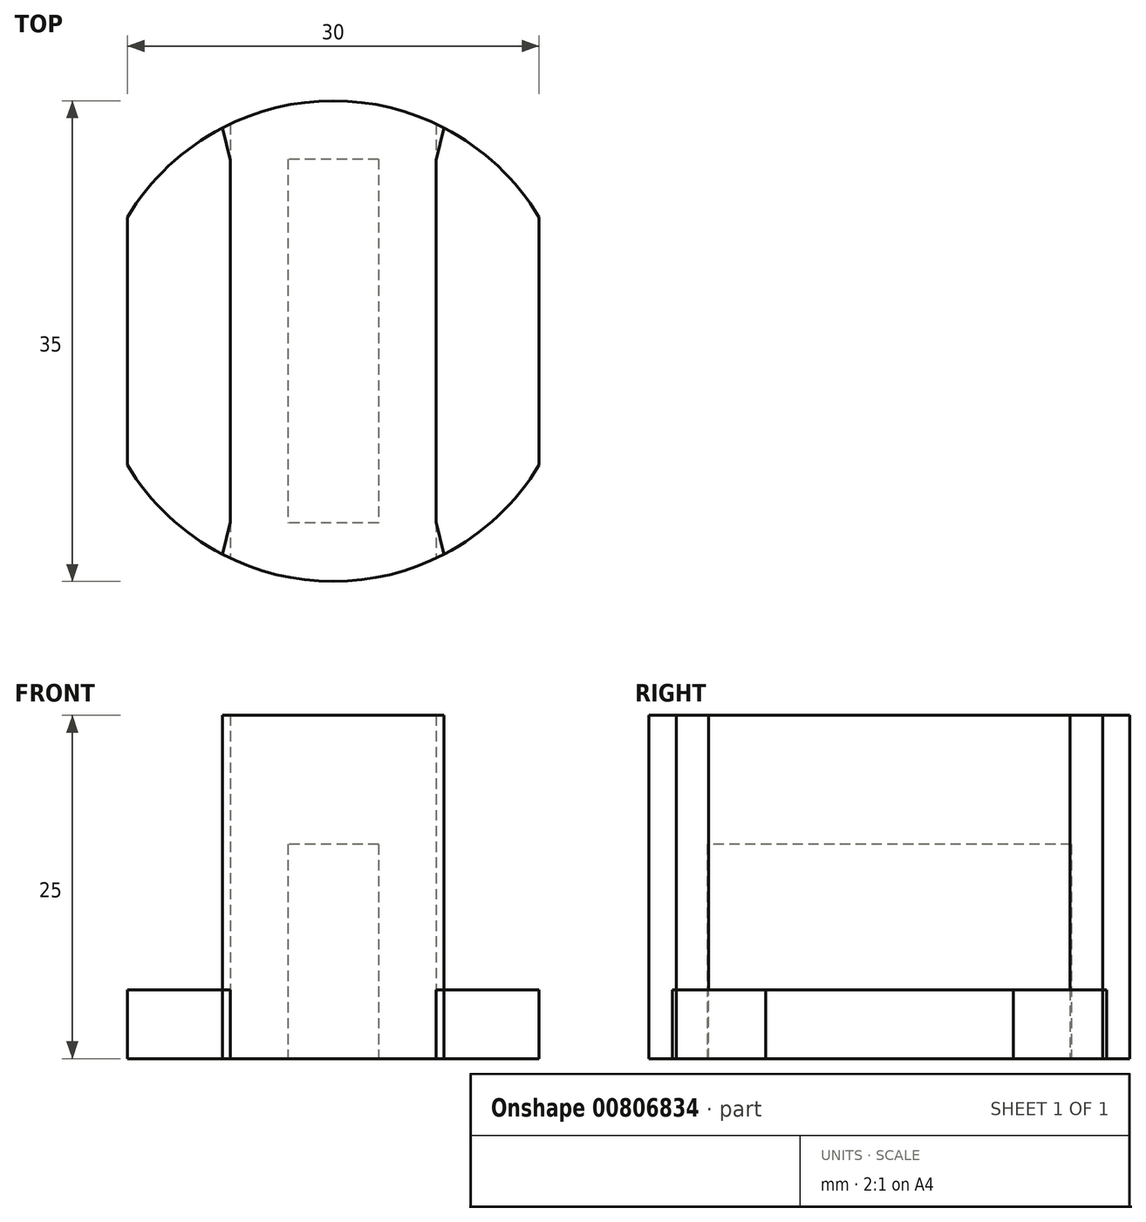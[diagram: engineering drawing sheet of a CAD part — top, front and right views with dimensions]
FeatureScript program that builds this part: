
annotation { "Feature Type Name" : "Feature", "Feature Type Description" : "" }
export const myFeature = defineFeature(function(context is Context, id is Id, definition is map)
    precondition{}
    {
        {
            var Q0;
            Q0=qCreatedBy(makeId("Top.planeOp"),FACE);
            var sketch = newSketch(context, id + "F0", { "sketchPlane" : qUnion([Q0])});
            skCircle(sketch, "E0", {"center": v(0, 0) * mm, "radius": 17.5 * mm});
            skLineSegment(sketch, "E1.bottom", {"start": v(7.5, 20) * mm, "end": v(-7.5, 20) * mm});
            skLineSegment(sketch, "E1.top", {"start": v(7.5, -20) * mm, "end": v(-7.5, -20) * mm});
            skLineSegment(sketch, "E1.left", {"start": v(7.5, 20) * mm, "end": v(7.5, -20) * mm});
            skLineSegment(sketch, "E1.right", {"start": v(-7.5, 20) * mm, "end": v(-7.5, -20) * mm});
            skLineSegment(sketch, "E2.bottom", {"start": v(3.3, 13.25) * mm, "end": v(-3.3, 13.25) * mm});
            skLineSegment(sketch, "E2.top", {"start": v(3.3, -13.25) * mm, "end": v(-3.3, -13.25) * mm});
            skLineSegment(sketch, "E2.left", {"start": v(3.3, 13.25) * mm, "end": v(3.3, -13.25) * mm});
            skLineSegment(sketch, "E2.right", {"start": v(-3.3, 13.25) * mm, "end": v(-3.3, -13.25) * mm});
            skLineSegment(sketch, "E3.bottom", {"start": v(15, 20) * mm, "end": v(-15, 20) * mm});
            skLineSegment(sketch, "E3.top", {"start": v(15, -20) * mm, "end": v(-15, -20) * mm});
            skLineSegment(sketch, "E3.left", {"start": v(15, 20) * mm, "end": v(15, -20) * mm});
            skLineSegment(sketch, "E3.right", {"start": v(-15, 20) * mm, "end": v(-15, -20) * mm});
            skLineSegment(sketch, "E4.bottom", {"start": v(23.86, 11.75) * mm, "end": v(-23.86, 11.75) * mm});
            skLineSegment(sketch, "E4.top", {"start": v(23.86, -11.75) * mm, "end": v(-23.86, -11.75) * mm});
            skLineSegment(sketch, "E4.left", {"start": v(23.86, 11.75) * mm, "end": v(23.86, -11.75) * mm});
            skLineSegment(sketch, "E4.right", {"start": v(-23.86, 11.75) * mm, "end": v(-23.86, -11.75) * mm});
            skSolve(sketch);
        }
        {
            var Q0;
            {var subQ0=sQuery(id+"F0.wireOp",EDGE,"E3.left");var subQ1=sQuery(id+"F0.wireOp",EDGE,"E0");var subQ2=makeQuery(id+"F0.imprint","INTERSECT",VERTEX,{"disambiguationData":[OD(0.0)],"derivedFrom":[subQ1,subQ0]});Q0=makeQuery(id+"F0.imprint","IMPRINT",FACE,{"disambiguationData":[TD([[makeQuery(id+"F0.imprint","IMPRINT",EDGE,{"disambiguationData":[TD([[subQ2,-1.0]])],"derivedFrom":subQ1}),1.0]])]});}
            var Q1;
            {var subQ0=sQuery(id+"F0.wireOp",EDGE,"E3.right");var subQ1=sQuery(id+"F0.wireOp",EDGE,"E0");var subQ2=makeQuery(id+"F0.imprint","INTERSECT",VERTEX,{"disambiguationData":[OD(0.0)],"derivedFrom":[subQ1,subQ0]});Q1=makeQuery(id+"F0.imprint","IMPRINT",FACE,{"disambiguationData":[TD([[makeQuery(id+"F0.imprint","IMPRINT",EDGE,{"disambiguationData":[TD([[subQ2,1.0]])],"derivedFrom":subQ1}),1.0]])]});}
            var Q2;
            {var subQ0=sQuery(id+"F0.wireOp",EDGE,"E1.right");var subQ1=sQuery(id+"F0.wireOp",EDGE,"E0");var subQ2=makeQuery(id+"F0.imprint","INTERSECT",VERTEX,{"disambiguationData":[OD(0.0)],"derivedFrom":[subQ1,subQ0]});Q2=makeQuery(id+"F0.imprint","IMPRINT",FACE,{"disambiguationData":[TD([[makeQuery(id+"F0.imprint","IMPRINT",EDGE,{"disambiguationData":[TD([[subQ2,-1.0]])],"derivedFrom":subQ1}),1.0]])]});}
            var Q3;
            {var subQ0=sQuery(id+"F0.wireOp",EDGE,"E1.left");var subQ1=sQuery(id+"F0.wireOp",EDGE,"E0");var subQ2=makeQuery(id+"F0.imprint","INTERSECT",VERTEX,{"disambiguationData":[OD(1.0)],"derivedFrom":[subQ1,subQ0]});Q3=makeQuery(id+"F0.imprint","IMPRINT",FACE,{"disambiguationData":[TD([[makeQuery(id+"F0.imprint","IMPRINT",EDGE,{"disambiguationData":[TD([[subQ2,-1.0]])],"derivedFrom":subQ1}),1.0]])]});}
            var Q4;
            {var subQ0=sQuery(id+"F0.wireOp",EDGE,"E4.top");var subQ1=sQuery(id+"F0.wireOp",EDGE,"E0");var subQ2=makeQuery(id+"F0.imprint","INTERSECT",VERTEX,{"disambiguationData":[OD(0.0)],"derivedFrom":[subQ1,subQ0]});Q4=makeQuery(id+"F0.imprint","IMPRINT",FACE,{"disambiguationData":[TD([[makeQuery(id+"F0.imprint","IMPRINT",EDGE,{"disambiguationData":[TD([[subQ2,-1.0]])],"derivedFrom":subQ1}),1.0]])]});}
            var Q5;
            {var subQ0=sQuery(id+"F0.wireOp",EDGE,"E4.bottom");var subQ1=sQuery(id+"F0.wireOp",EDGE,"E0");var subQ2=makeQuery(id+"F0.imprint","INTERSECT",VERTEX,{"disambiguationData":[OD(0.0)],"derivedFrom":[subQ1,subQ0]});Q5=makeQuery(id+"F0.imprint","IMPRINT",FACE,{"disambiguationData":[TD([[makeQuery(id+"F0.imprint","IMPRINT",EDGE,{"disambiguationData":[TD([[subQ2,-1.0]])],"derivedFrom":subQ1}),1.0]])]});}
            extrude(context, id + "F1", {"entities" : qUnion([Q0, Q1, Q2, Q3, Q4, Q5]), "depth" : 5 * mm, "offsetDistance" : 25 * mm});
        }
        {
            var Q0;
            Q0=makeQuery(id+"F0.imprint","IMPRINT",FACE,{"disambiguationData":[TD([[makeQuery(id+"F0.imprint","IMPRINT",EDGE,{"derivedFrom":sQuery(id+"F0.wireOp",EDGE,"E2.bottom")}),1.0]])]});
            var Q1;
            Q1=makeQuery(id+"F0.imprint","IMPRINT",FACE,{"disambiguationData":[TD([[makeQuery(id+"F0.imprint","IMPRINT",EDGE,{"derivedFrom":sQuery(id+"F0.wireOp",EDGE,"E2.bottom")}),-1.0]])]});
            var Q2;
            {var subQ0=sQuery(id+"F0.wireOp",EDGE,"E4.bottom");var subQ1=sQuery(id+"F0.wireOp",EDGE,"E1.right");var subQ2=makeQuery(id+"F0.imprint","INTERSECT",VERTEX,{"derivedFrom":[subQ1,subQ0]});Q2=makeQuery(id+"F0.imprint","IMPRINT",FACE,{"disambiguationData":[TD([[makeQuery(id+"F0.imprint","IMPRINT",EDGE,{"disambiguationData":[TD([[subQ2,-1.0]])],"derivedFrom":subQ1}),1.0]])]});}
            var Q3;
            {var subQ9=sQuery(id+"F0.wireOp",EDGE,"E2.top");Q3=makeQuery(id+"F0.imprint","IMPRINT",FACE,{"disambiguationData":[TD([[makeQuery(id+"F0.imprint","IMPRINT",EDGE,{"derivedFrom":subQ9}),1.0]])]});}
            var Q4;
            {var subQ0=sQuery(id+"F0.wireOp",EDGE,"E4.bottom");var subQ1=sQuery(id+"F0.wireOp",EDGE,"E1.left");var subQ2=makeQuery(id+"F0.imprint","INTERSECT",VERTEX,{"derivedFrom":[subQ1,subQ0]});Q4=makeQuery(id+"F0.imprint","IMPRINT",FACE,{"disambiguationData":[TD([[makeQuery(id+"F0.imprint","IMPRINT",EDGE,{"disambiguationData":[TD([[subQ2,-1.0]])],"derivedFrom":subQ1}),-1.0]])]});}
            var Q5;
            {var subQ0=sQuery(id+"F0.wireOp",EDGE,"E4.bottom");var subQ1=sQuery(id+"F0.wireOp",EDGE,"E2.left");var subQ2=makeQuery(id+"F0.imprint","INTERSECT",VERTEX,{"derivedFrom":[subQ1,subQ0]});Q5=makeQuery(id+"F0.imprint","IMPRINT",FACE,{"disambiguationData":[TD([[makeQuery(id+"F0.imprint","IMPRINT",EDGE,{"disambiguationData":[TD([[subQ2,-1.0]])],"derivedFrom":subQ1}),-1.0]])]});}
            var Q6;
            {var subQ0=sQuery(id+"F0.wireOp",EDGE,"E2.top");Q6=makeQuery(id+"F0.imprint","IMPRINT",FACE,{"disambiguationData":[TD([[makeQuery(id+"F0.imprint","IMPRINT",EDGE,{"derivedFrom":subQ0}),-1.0]])]});}
            var Q7;
            {var subQ0=sQuery(id+"F0.wireOp",EDGE,"E4.top");var subQ1=sQuery(id+"F0.wireOp",EDGE,"E0");var subQ2=makeQuery(id+"F0.imprint","INTERSECT",VERTEX,{"disambiguationData":[OD(0.0)],"derivedFrom":[subQ1,subQ0]});Q7=makeQuery(id+"F0.imprint","IMPRINT",FACE,{"disambiguationData":[TD([[makeQuery(id+"F0.imprint","IMPRINT",EDGE,{"disambiguationData":[TD([[subQ2,-1.0]])],"derivedFrom":subQ1}),1.0]])]});}
            var Q8;
            {var subQ0=sQuery(id+"F0.wireOp",EDGE,"E1.right");var subQ1=sQuery(id+"F0.wireOp",EDGE,"E0");var subQ2=makeQuery(id+"F0.imprint","INTERSECT",VERTEX,{"disambiguationData":[OD(0.0)],"derivedFrom":[subQ1,subQ0]});Q8=makeQuery(id+"F0.imprint","IMPRINT",FACE,{"disambiguationData":[TD([[makeQuery(id+"F0.imprint","IMPRINT",EDGE,{"disambiguationData":[TD([[subQ2,-1.0]])],"derivedFrom":subQ1}),1.0]])]});}
            var Q9;
            {var subQ0=sQuery(id+"F0.wireOp",EDGE,"E4.bottom");var subQ1=sQuery(id+"F0.wireOp",EDGE,"E0");var subQ2=makeQuery(id+"F0.imprint","INTERSECT",VERTEX,{"disambiguationData":[OD(0.0)],"derivedFrom":[subQ1,subQ0]});Q9=makeQuery(id+"F0.imprint","IMPRINT",FACE,{"disambiguationData":[TD([[makeQuery(id+"F0.imprint","IMPRINT",EDGE,{"disambiguationData":[TD([[subQ2,-1.0]])],"derivedFrom":subQ1}),1.0]])]});}
            var Q10;
            {var subQ0=sQuery(id+"F0.wireOp",EDGE,"E1.left");var subQ1=sQuery(id+"F0.wireOp",EDGE,"E0");var subQ2=makeQuery(id+"F0.imprint","INTERSECT",VERTEX,{"disambiguationData":[OD(1.0)],"derivedFrom":[subQ1,subQ0]});Q10=makeQuery(id+"F0.imprint","IMPRINT",FACE,{"disambiguationData":[TD([[makeQuery(id+"F0.imprint","IMPRINT",EDGE,{"disambiguationData":[TD([[subQ2,-1.0]])],"derivedFrom":subQ1}),1.0]])]});}
            extrude(context, id + "F2", {"entities" : qUnion([Q0, Q1, Q2, Q3, Q4, Q5, Q6, Q7, Q8, Q9, Q10]), "depth" : 25 * mm, "offsetDistance" : 25 * mm});
        }
        {
            var Q0;
            Q0=makeQuery(id+"F0.imprint","IMPRINT",FACE,{"disambiguationData":[TD([[makeQuery(id+"F0.imprint","IMPRINT",EDGE,{"derivedFrom":sQuery(id+"F0.wireOp",EDGE,"E2.bottom")}),1.0]])]});
            var Q1;
            {var subQ0=sQuery(id+"F0.wireOp",EDGE,"E4.bottom");var subQ1=sQuery(id+"F0.wireOp",EDGE,"E2.left");var subQ2=makeQuery(id+"F0.imprint","INTERSECT",VERTEX,{"derivedFrom":[subQ1,subQ0]});Q1=makeQuery(id+"F0.imprint","IMPRINT",FACE,{"disambiguationData":[TD([[makeQuery(id+"F0.imprint","IMPRINT",EDGE,{"disambiguationData":[TD([[subQ2,-1.0]])],"derivedFrom":subQ1}),-1.0]])]});}
            var Q2;
            {var subQ0=sQuery(id+"F0.wireOp",EDGE,"E2.top");Q2=makeQuery(id+"F0.imprint","IMPRINT",FACE,{"disambiguationData":[TD([[makeQuery(id+"F0.imprint","IMPRINT",EDGE,{"derivedFrom":subQ0}),-1.0]])]});}
            extrude(context, id + "F3", {"entities" : qUnion([Q0, Q1, Q2]), "operationType" : NewBodyOperationType.REMOVE, "oppositeDirection" : true, "depth" : -15.6 * mm, "offsetDistance" : 25 * mm});
        }
        {
            var Q0;
            {var subQ0=sQuery(id+"F0.wireOp",EDGE,"E4.top");var subQ1=sQuery(id+"F0.wireOp",EDGE,"E0");Q0=makeQuery(id+"F2.opExtrude","SWEPT_EDGE",EDGE,{"disambiguationData":[OSD([subQ1,subQ0]),TDD([makeQuery(id+"F0.imprint","INTERSECT",VERTEX,{"disambiguationData":[OD(0.0)],"derivedFrom":[subQ1,subQ0]})])]});}
            var Q1;
            {var subQ0=sQuery(id+"F0.wireOp",EDGE,"E4.top");var subQ1=sQuery(id+"F0.wireOp",EDGE,"E0");Q1=makeQuery(id+"F2.opExtrude","SWEPT_EDGE",EDGE,{"disambiguationData":[OSD([subQ1,subQ0]),TDD([makeQuery(id+"F0.imprint","INTERSECT",VERTEX,{"disambiguationData":[OD(1.0)],"derivedFrom":[subQ1,subQ0]})])]});}
            var Q2;
            {var subQ0=sQuery(id+"F0.wireOp",EDGE,"E4.bottom");var subQ1=sQuery(id+"F0.wireOp",EDGE,"E0");Q2=makeQuery(id+"F2.opExtrude","SWEPT_EDGE",EDGE,{"disambiguationData":[OSD([subQ1,subQ0]),TDD([makeQuery(id+"F0.imprint","INTERSECT",VERTEX,{"disambiguationData":[OD(0.0)],"derivedFrom":[subQ1,subQ0]})])]});}
            var Q3;
            {var subQ0=sQuery(id+"F0.wireOp",EDGE,"E4.bottom");var subQ1=sQuery(id+"F0.wireOp",EDGE,"E0");Q3=makeQuery(id+"F2.opExtrude","SWEPT_EDGE",EDGE,{"disambiguationData":[OSD([subQ1,subQ0]),TDD([makeQuery(id+"F0.imprint","INTERSECT",VERTEX,{"disambiguationData":[OD(1.0)],"derivedFrom":[subQ1,subQ0]})])]});}
            chamfer(context, id + "F4", {"entities" : qUnion([Q0, Q1, Q2, Q3]), "width" : 2 * mm, "tangentPropagation" : true});
        }
    });
